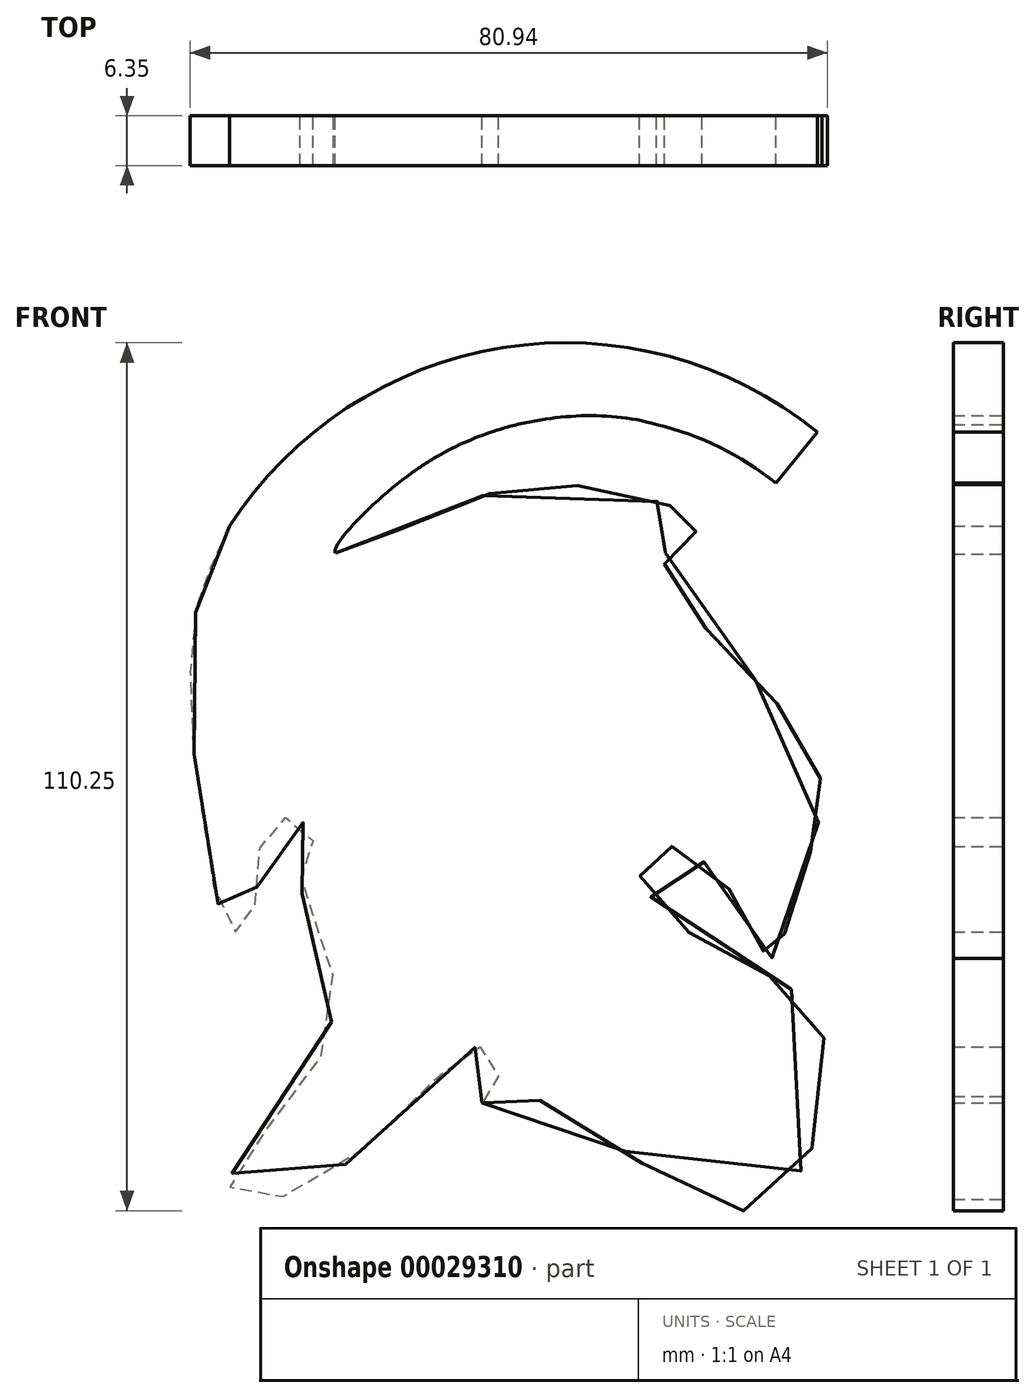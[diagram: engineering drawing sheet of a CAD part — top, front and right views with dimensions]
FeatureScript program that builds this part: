
annotation { "Feature Type Name" : "Feature", "Feature Type Description" : "" }
export const myFeature = defineFeature(function(context is Context, id is Id, definition is map)
    precondition{}
    {
        {
            var Q0;
            Q0=qCreatedBy(makeId("Front.planeOp"),FACE);
            var sketch = newSketch(context, id + "F0", { "sketchPlane" : qUnion([Q0])});
            skArc(sketch, "E0", {"start": v(26.61, 63.08) * mm, "mid": v(-13.38, 73.75) * mm, "end": v(-48.04, 51.12) * mm});
            skArc(sketch, "E1", {"start": v(21.34, 56.56) * mm, "mid": v(-8.6, 64.58) * mm, "end": v(-34.58, 47.7) * mm});
            skFitSpline(sketch, "E2", {"points": [v(-48.04, 51.12) * mm, v(-50.7, 45.3) * mm, v(-52.39, 40.22) * mm, v(-52.95, 26.67) * mm, v(-51.26, 12.84) * mm, v(-48.04, 0) * mm, v(-45.9, 0) * mm, v(-44.48, 6.91) * mm, v(-42.5, 13.69) * mm, v(-38, 12.84) * mm, v(-38, 8.9) * mm, v(-39.12, 5.5) * mm, v(-36.58, 0) * mm, v(-36.86, -17.07) * mm, v(-48.04, -32.6) * mm, v(-38.56, -33.16) * mm, v(-18.8, -16.23) * mm, v(-15.42, -15.38) * mm, v(-14, -19.33) * mm, v(-15.98, -22.15) * mm, v(-9.49, -21.6) * mm, v(18.73, -35.7) * mm, v(27.2, -13.12) * mm, v(12.8, -2.12) * mm, v(4.06, 7.76) * mm, v(8.86, 10.3) * mm, v(18.45, 0) * mm, v(20.7, -3.81) * mm, v(24.94, 7.2) * mm, v(26.35, 21.3) * mm, v(11.11, 39.65) * mm, v(7.73, 48.4) * mm, v(11.96, 51.12) * mm, v(0, 55.74) * mm, v(-20.21, 53.48) * mm, v(-34.58, 47.7) * mm, v(-25.5, 57.42) * mm, v(-8.6, 64.58) * mm, v(6.2, 64.01) * mm, v(21.34, 56.56) * mm], "startDerivative": vector(-142.09, -310.22) * mm, "endDerivative": vector(467.4, -279.17) * mm});
            skLineSegment(sketch, "E3", {"start": v(21.34, 56.56) * mm, "end": v(26.61, 63.08) * mm});
            skSolve(sketch);
        }
        {
            var Q0;
            {var subQ9=sQuery(id+"F0.wireOp",EDGE,"E0");Q0=makeQuery(id+"F0.imprint","IMPRINT",FACE,{"disambiguationData":[TD([[makeQuery(id+"F0.imprint","IMPRINT",EDGE,{"derivedFrom":subQ9}),1.0]])]});}
            extrude(context, id + "F1", {"entities" : qUnion([Q0]), "depth" : 6.35 * mm});
        }
        {
            var Q0;
            Q0=makeQuery(id+"F1.opExtrude","CAP_FACE",FACE,{"disambiguationData":[OSD([sQuery(id+"F0.wireOp",EDGE,"E0"),sQuery(id+"F0.wireOp",EDGE,"E1"),sQuery(id+"F0.wireOp",EDGE,"E2"),sQuery(id+"F0.wireOp",EDGE,"E3")])],"isStart":false});
            var sketch = newSketch(context, id + "F2", { "sketchPlane" : qUnion([Q0])});
            skFitSpline(sketch, "E4", {"points": [v(22.89, -33.04) * mm, v(20.24, -28.45) * mm, v(8.73, -20.03) * mm, v(20.52, -29.3) * mm, v(22.89, -33.04) * mm]});
            skFitSpline(sketch, "E5", {"points": [v(26.97, -27.05) * mm, v(23.89, -22.84) * mm, v(13.5, -15.26) * mm, v(24.73, -23.4) * mm, v(26.97, -27.05) * mm]});
            skSolve(sketch);
        }
    });
